# Revit family: Шкаф телекоммуникационный напольный 600х600
name_source: partatom
category: Обобщенные модели
units: mm (PartAtom-declared; Revit-internal decimal feet)

## family parameters
Всегда вертикально = Да
Может служить основой для арматурных стержней = Нет
На основе рабочей плоскости = Нет
Общий = Нет
При загрузке вырезать с полостями = Нет
Размер круглого соединителя = Использовать диаметр
Тип детали = Нормальный
Точка расчета площади = Нет

## types (36) — shared parameters
ADSK_URL страницы изделия = https://www.ssd.ru
ADSK_Единица измерения = шт
ADSK_Завод-изготовитель = АО СВЯЗЬСТРОЙДЕТАЛЬ
ADSK_Зона = -
ADSK_Обозначение = -
ADSK_Предел огнестойкости = -
Материал крепежей = Металл
zero-valued in all types: Ноль

## per-type parameters (varying)
| type | ADSK_Код изделия | ADSK_Масса_Текст | ADSK_Наименование | ADSK_Размер_Высота | Материал каркаса | Материал колес и ручек | Описание | Тип шкафа |
| ШТ-НП-18U-600-600-М | 130411-00493 | 50 | Шкаф телекоммуникационный напольный 19 18U(600x600) ШТ-НП-18U-600-600-М передняя дверь металл ССД | 972 мм | Металл белый | Металл черный | Шкаф телекоммуникационный напольный 19 18U(600x600) ШТ-НП-18U-600-600-М передняя дверь металл ССД | Дверь : Металическая дверь белая |
| ШТ-НП-24U-600-600-М | 130411-00502 | 58 | Шкаф телекоммуникационный напольный 19 24U(600x600) ШТ-НП-24U-600-600-М передняя дверь металл ССД | 1239 мм | Металл белый | Металл черный | Шкаф телекоммуникационный напольный 19 24U(600x600) ШТ-НП-24U-600-600-М передняя дверь металл ССД | Дверь : Металическая дверь белая |
| ШТ-НП-27U-600-600-М | 130411-00511 | 62 | Шкаф телекоммуникационный напольный 19 27U(600x600) ШТ-НП-27U-600-600-М передняя дверь металл ССД | 1372 мм | Металл белый | Металл черный | Шкаф телекоммуникационный напольный 19 27U(600x600) ШТ-НП-27U-600-600-М передняя дверь металл ССД | Дверь : Металическая дверь белая |
| ШТ-НП-33U-600-600-М | 130411-00520 | 71 | Шкаф телекоммуникационный напольный 19 33U(600x600) ШТ-НП-33U-600-600-М передняя дверь металл ССД | 1639 мм | Металл белый | Металл черный | Шкаф телекоммуникационный напольный 19 33U(600x600) ШТ-НП-33U-600-600-М передняя дверь металл ССД | Дверь : Металическая дверь белая |
| ШТ-НП-42U-600-600-М | 130411-00528 | 83 | Шкаф телекоммуникационный напольный 19 42U(600x600) ШТ-НП-42U-600-600-М передняя дверь металл ССД | 2039 мм | Металл белый | Металл черный | Шкаф телекоммуникационный напольный 19 42U(600x600) ШТ-НП-42U-600-600-М передняя дверь металл ССД | Дверь : Металическая дверь белая |
| ШТ-НП-47U-600-600-М | 130411-00537 | 90 | Шкаф телекоммуникационный напольный 19 47U(600x600) ШТ-НП-47U-600-600-М передняя дверь металл ССД | 2261 мм | Металл белый | Металл черный | Шкаф телекоммуникационный напольный 19 47U(600x600) ШТ-НП-47U-600-600-М передняя дверь металл ССД | Дверь : Металическая дверь белая |
| ШТ-НП-18U-600-600-П | 130411-00494 | 49 | Шкаф телекоммуникационный напольный 19 18U(600x600) ШТ-НП-18U-600-600-П передняя дверь перфорированная ССД | 972 мм | Металл белый | Металл черный | Шкаф телекоммуникационный напольный 19 18U(600x600) ШТ-НП-18U-600-600-П передняя дверь перфорированная ССД | Дверь : Перфарированная дверь |
| ШТ-НП-24U-600-600-П | 130411-00503 | 76 | Шкаф телекоммуникационный напольный 19 24U(600x600) ШТ-НП-24U-600-600-П передняя дверь перф ССД | 1239 мм | Металл белый | Металл черный | Шкаф телекоммуникационный напольный 19 24U(600x600) ШТ-НП-24U-600-600-П передняя дверь перф ССД | Дверь : Перфарированная дверь |
| ШТ-НП-27U-600-600-П | 130411-00512 | 60 | Шкаф телекоммуникационный напольный 19 27U(600x600) ШТ-НП-27U-600-600-П передняя дверь перфорированная ССД | 1372 мм | Металл белый | Металл черный | Шкаф телекоммуникационный напольный 19 27U(600x600) ШТ-НП-27U-600-600-П передняя дверь перфорированная ССД | Дверь : Перфарированная дверь |
| ШТ-НП-33U-600-600-П | 130411-00521 | 70 | Шкаф телекоммуникационный напольный 19 33U(600x600) ШТ-НП-33U-600-600-П передняя дверь перфорированная ССД | 1639 мм | Металл белый | Металл черный | Шкаф телекоммуникационный напольный 19 33U(600x600) ШТ-НП-33U-600-600-П передняя дверь перфорированная ССД | Дверь : Перфарированная дверь |
| ШТ-НП-42U-600-600-П | 130411-00529 | 78 | Шкаф телекоммуникационный напольный 19 42U(600x600) ШТ-НП-42U-600-600-П передняя дверь перфорированная ССД | 2039 мм | Металл белый | Металл черный | Шкаф телекоммуникационный напольный 19 42U(600x600) ШТ-НП-42U-600-600-П передняя дверь перфорированная ССД | Дверь : Перфарированная дверь |
| ШТ-НП-47U-600-600-П | 130411-00538 | 86 | Шкаф телекоммуникационный напольный 19 47U(600x600) ШТ-НП-47U-600-600-П передняя дверь перфорированная ССД | 2261 мм | Металл белый | Металл черный | Шкаф телекоммуникационный напольный 19 47U(600x600) ШТ-НП-47U-600-600-П передняя дверь перфорированная ССД | Дверь : Перфарированная дверь |
| ШТ-НП-18U-600-600-С | 130411-00492 | 52 | Шкаф телекоммуникационный напольный 19 18U(600x600) ШТ-НП-18U-600-600-С передняя дверь стекло ССД | 972 мм | Металл белый | Металл черный | Шкаф телекоммуникационный напольный 19 18U(600x600) ШТ-НП-18U-600-600-С передняя дверь стекло ССД | Дверь : Стеклянная дверь |
| ШТ-НП-24U-600-600-С | 130411-00501 | 60 | Шкаф телекоммуникационный напольный 19 24U(600x600) ШТ-НП-24U-600-600-С передняя дверь стекло ССД | 1239 мм | Металл белый | Металл черный | Шкаф телекоммуникационный напольный 19 24U(600x600) ШТ-НП-24U-600-600-С передняя дверь стекло ССД | Дверь : Стеклянная дверь |
| ШТ-НП-27U-600-600-С | 130411-00510 | 65 | Шкаф телекоммуникационный напольный 19 27U(600x600) ШТ-НП-27U-600-600-С передняя дверь стекло ССД | 1372 мм | Металл белый | Металл черный | Шкаф телекоммуникационный напольный 19 27U(600x600) ШТ-НП-27U-600-600-С передняя дверь стекло ССД | Дверь : Стеклянная дверь |
| ШТ-НП-33U-600-600-С | 130411-00519 | 74 | Шкаф телекоммуникационный напольный 19 33U(600x600) ШТ-НП-33U-600-600-С передняя дверь стекло ССД | 1639 мм | Металл белый | Металл черный | Шкаф телекоммуникационный напольный 19 33U(600x600) ШТ-НП-33U-600-600-С передняя дверь стекло ССД | Дверь : Стеклянная дверь |
| ШТ-НП-42U-600-600-С | 130411-00486 | 87 | Шкаф телекоммуникационный напольный 19 42U(600x600)  ШТ-НП-42U-600-600-С передняя дверь стекло ССД | 2039 мм | Металл белый | Металл черный | Шкаф телекоммуникационный напольный 19 42U(600x600)  ШТ-НП-42U-600-600-С передняя дверь стекло ССД | Дверь : Стеклянная дверь |
| ШТ-НП-47U-600-600-С | 130411-00536 | 95 | Шкаф телекоммуникационный напольный 19 47U(600x600) ШТ-НП-47U-600-600-С передняя дверь стекло ССД | 2261 мм | Металл белый | Металл черный | Шкаф телекоммуникационный напольный 19 47U(600x600) ШТ-НП-47U-600-600-С передняя дверь стекло ССД | Дверь : Стеклянная дверь |
| ШТ-НП-18U-600-600-М-Ч | 130411-01128 | 50 | Шкаф телекоммуникационный напольный 19 18U(600x600) ШТ-НП-18U-600-600-М передняя дверь металл черная ССД | 972 мм | Металл черный | Металл белый | Шкаф телекоммуникационный напольный 19 18U(600x600) ШТ-НП-18U-600-600-М передняя дверь металл черная ССД | Дверь : Металлическая дверь черная |
| ШТ-НП-24U-600-600-М-Ч | 130411-01131 | 58 | Шкаф телекоммуникационный напольный 19 24U(600x600) ШТ-НП-24U-600-600-М передняя дверь металл черная ССД | 1239 мм | Металл черный | Металл белый | Шкаф телекоммуникационный напольный 19 24U(600x600) ШТ-НП-24U-600-600-М передняя дверь металл черная ССД | Дверь : Металлическая дверь черная |
| ШТ-НП-27U-600-600-М-Ч | 130411-01135 | 62 | Шкаф телекоммуникационный напольный 19 27U(600x600) ШТ-НП-27U-600-600-М передняя дверь металл черная ССД | 1372 мм | Металл черный | Металл белый | Шкаф телекоммуникационный напольный 19 27U(600x600) ШТ-НП-27U-600-600-М передняя дверь металл черная ССД | Дверь : Металлическая дверь черная |
| ШТ-НП-33U-600-600-М-Ч | 130411-01138 | 71 | Шкаф телекоммуникационный напольный 19 33U(600x600) ШТ-НП-33U-600-600-М передняя дверь металл черная ССД | 1639 мм | Металл черный | Металл белый | Шкаф телекоммуникационный напольный 19 33U(600x600) ШТ-НП-33U-600-600-М передняя дверь металл черная ССД | Дверь : Металлическая дверь черная |
| ШТ-НП-42U-600-600-М-Ч | 130411-01139 | 83 | Шкаф телекоммуникационный напольный 19 42U(600x600) ШТ-НП-42U-600-600-М передняя дверь металл черная ССД | 2039 мм | Металл черный | Металл белый | Шкаф телекоммуникационный напольный 19 42U(600x600) ШТ-НП-42U-600-600-М передняя дверь металл черная ССД | Дверь : Металлическая дверь черная |
| ШТ-НП-47U-600-600-М-Ч | 130411-01145 | 90 | Шкаф телекоммуникационный напольный 19 47U(600x600) ШТ-НП-47U-600-600-М передняя дверь металл черная ССД | 2261 мм | Металл черный | Металл белый | Шкаф телекоммуникационный напольный 19 47U(600x600) ШТ-НП-47U-600-600-М передняя дверь металл черная ССД | Дверь : Металлическая дверь черная |
| ШТ-НП-18U-600-600-П-Ч | 130411-01129 | 49 | Шкаф телекоммуникационный напольный 19 18U(600x600) ШТ-НП-18U-600-600-П передняя дверь перфорированная  черная ССД | 972 мм | Металл черный | Металл белый | Шкаф телекоммуникационный напольный 19 18U(600x600) ШТ-НП-18U-600-600-П передняя дверь перфорированная  черная ССД | Дверь : Перфарированная дверь |
| ШТ-НП-24U-600-600-П-Ч | 130411-01132 | 76 | Шкаф телекоммуникационный напольный 19 24U(600x600) ШТ-НП-24U-600-600-П передняя дверь перф черная ССД | 1239 мм | Металл черный | Металл белый | Шкаф телекоммуникационный напольный 19 24U(600x600) ШТ-НП-24U-600-600-П передняя дверь перф черная ССД | Дверь : Перфарированная дверь |
| ШТ-НП-27U-600-600-П-Ч | 130411-01133 | 60 | Шкаф телекоммуникационный напольный 19 27U(600x600) ШТ-НП-27U-600-600-П передняя дверь перфорированная черная ССД | 1372 мм | Металл черный | Металл белый | Шкаф телекоммуникационный напольный 19 27U(600x600) ШТ-НП-27U-600-600-П передняя дверь перфорированная черная ССД | Дверь : Перфарированная дверь |
| ШТ-НП-33U-600-600-П-Ч | 130411-01136 | 70 | Шкаф телекоммуникационный напольный 19 33U(600x600) ШТ-НП-33U-600-600-П передняя дверь перфорированная черная ССД | 1639 мм | Металл черный | Металл белый | Шкаф телекоммуникационный напольный 19 33U(600x600) ШТ-НП-33U-600-600-П передняя дверь перфорированная черная ССД | Дверь : Перфарированная дверь |
| ШТ-НП-42U-600-600-П-Ч | 130411-01142 | 78 | Шкаф телекоммуникационный напольный 19 42U(600x600) ШТ-НП-42U-600-600-П передняя дверь перфорированная черная ССД | 2039 мм | Металл черный | Металл белый | Шкаф телекоммуникационный напольный 19 42U(600x600) ШТ-НП-42U-600-600-П передняя дверь перфорированная черная ССД | Дверь : Перфарированная дверь |
| ШТ-НП-47U-600-600-П-Ч | 130411-01143 | 86 | Шкаф телекоммуникационный напольный 19 47U(600x600) ШТ-НП-47U-600-600-П передняя дверь перфорированная черная ССД | 2261 мм | Металл черный | Металл белый | Шкаф телекоммуникационный напольный 19 47U(600x600) ШТ-НП-47U-600-600-П передняя дверь перфорированная черная ССД | Дверь : Перфарированная дверь |
| ШТ-НП-18U-600-600-С-Ч | 130411-01127 | 52 | Шкаф телекоммуникационный напольный 19 18U(600x600) ШТ-НП-18U-600-600-С передняя дверь стекло черная ССД | 972 мм | Металл черный | Металл белый | Шкаф телекоммуникационный напольный 19 18U(600x600) ШТ-НП-18U-600-600-С передняя дверь стекло черная ССД | Дверь : Стеклянная дверь |
| ШТ-НП-24U-600-600-С-Ч | 130411-01130 | 60 | Шкаф телекоммуникационный напольный 19 24U(600x600) ШТ-НП-24U-600-600-С передняя дверь стекло черная ССД | 1239 мм | Металл черный | Металл белый | Шкаф телекоммуникационный напольный 19 24U(600x600) ШТ-НП-24U-600-600-С передняя дверь стекло черная ССД | Дверь : Стеклянная дверь |
| ШТ-НП-27U-600-600-С-Ч | 130411-01134 | 65 | Шкаф телекоммуникационный напольный 19 27U(600x600) ШТ-НП-27U-600-600-С передняя дверь стекло черная ССД | 1372 мм | Металл черный | Металл белый | Шкаф телекоммуникационный напольный 19 27U(600x600) ШТ-НП-27U-600-600-С передняя дверь стекло черная ССД | Дверь : Стеклянная дверь |
| ШТ-НП-33U-600-600-С-Ч | 130411-01140 | 74 | Шкаф телекоммуникационный напольный 19 33U(600x600) ШТ-НП-33U-600-600-С передняя дверь стекло  черная ССД | 1639 мм | Металл черный | Металл белый | Шкаф телекоммуникационный напольный 19 33U(600x600) ШТ-НП-33U-600-600-С передняя дверь стекло  черная ССД | Дверь : Стеклянная дверь |
| ШТ-НП-42U-600-600-С-Ч | 130411-01141 | 87 | Шкаф телекоммуникационный напольный 19 42U(600x600)  ШТ-НП-42U-600-600-С передняя дверь стекло  черная ССД | 2039 мм | Металл черный | Металл белый | Шкаф телекоммуникационный напольный 19 42U(600x600)  ШТ-НП-42U-600-600-С передняя дверь стекло  черная ССД | Дверь : Стеклянная дверь |
| ШТ-НП-47U-600-600-С-Ч | 130411-01144 | 95 | Шкаф телекоммуникационный напольный 19 47U(600x600) ШТ-НП-47U-600-600-С передняя дверь стекло черная ССД | 2261 мм | Металл черный | Металл белый | Шкаф телекоммуникационный напольный 19 47U(600x600) ШТ-НП-47U-600-600-С передняя дверь стекло черная ССД | Дверь : Стеклянная дверь |

note: column(s) folded — value = type name in every type: ADSK_Наименование краткое
